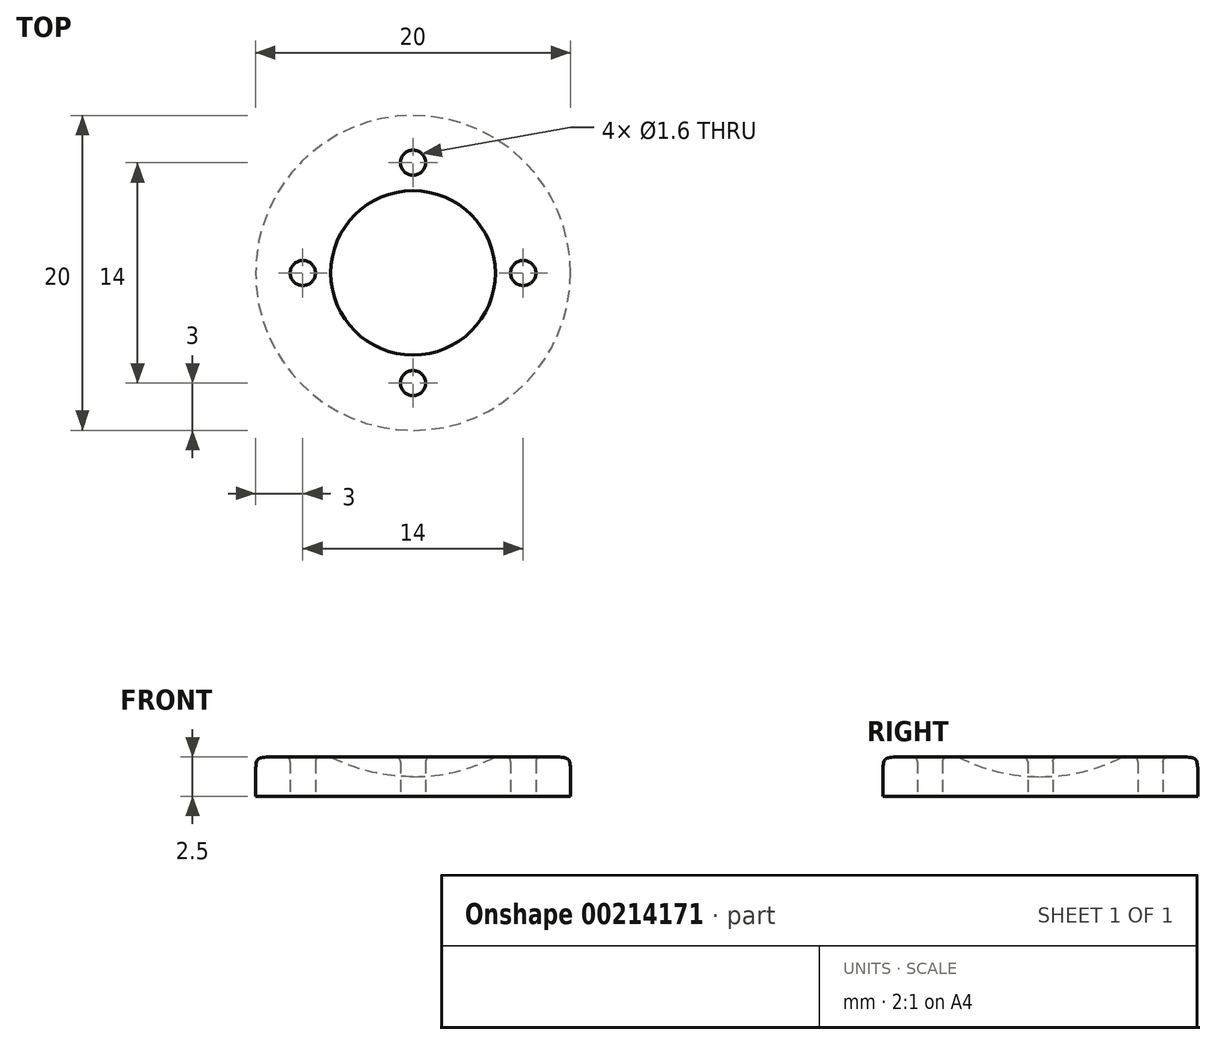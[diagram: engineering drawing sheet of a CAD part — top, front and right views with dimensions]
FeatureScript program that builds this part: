
annotation { "Feature Type Name" : "Feature", "Feature Type Description" : "" }
export const myFeature = defineFeature(function(context is Context, id is Id, definition is map)
    precondition{}
    {
        {
            var Q0;
            Q0=qCreatedBy(makeId("Top.planeOp"),FACE);
            var sketch = newSketch(context, id + "F0", { "sketchPlane" : qUnion([Q0])});
            skCircle(sketch, "E0", {"center": v(0, 0) * mm, "radius": 10 * mm});
            skCircle(sketch, "E1", {"center": v(0, 0) * mm, "radius": 7 * mm, "construction": true});
            skCircle(sketch, "E2", {"center": v(-7, 0) * mm, "radius": 0.8 * mm});
            skCircle(sketch, "E3.1.0", {"center": v(0, -7) * mm, "radius": 0.8 * mm});
            skCircle(sketch, "E3.2.0", {"center": v(7, 0) * mm, "radius": 0.8 * mm});
            skCircle(sketch, "E4.1.3.0", {"center": v(0, 7) * mm, "radius": 0.8 * mm});
            skSolve(sketch);
        }
        {
            var Q0;
            Q0=makeQuery(id+"F0.imprint","IMPRINT",FACE,{"disambiguationData":[TD([[makeQuery(id+"F0.imprint","IMPRINT",EDGE,{"derivedFrom":sQuery(id+"F0.wireOp",EDGE,"E0")}),1.0]])]});
            extrude(context, id + "F1", {"entities" : qUnion([Q0]), "depth" : 2.5 * mm});
        }
        {
            var Q0;
            Q0=qCreatedBy(makeId("Front.planeOp"),FACE);
            var sketch = newSketch(context, id + "F2", { "sketchPlane" : qUnion([Q0])});
            skLineSegment(sketch, "E5.0", {"start": v(-10, 2.5) * mm, "end": v(10, 2.5) * mm});
            skLineSegment(sketch, "E6", {"start": v(-10, 2.5) * mm, "end": v(0, 12.8) * mm, "construction": true});
            skCircle(sketch, "E7", {"center": v(0, 12.8) * mm, "radius": 11.55 * mm});
            skLineSegment(sketch, "E8", {"start": v(0, 0) * mm, "end": v(0, 2.5) * mm, "construction": true});
            skLineSegment(sketch, "E9", {"start": v(0, 1.25) * mm, "end": v(2.32, 1.25) * mm, "construction": true});
            skPoint(sketch, "E9.endSnap0", {"position": v(0, 1.25) * mm});
            skLineSegment(sketch, "E10", {"start": v(0, 1.25) * mm, "end": v(0, 24.34) * mm});
            skSolve(sketch);
        }
        {
            var Q0;
            {var subQ0=sQuery(id+"F2.wireOp",EDGE,"E7");var subQ1=sQuery(id+"F2.wireOp",EDGE,"E5.0");var subQ2=makeQuery(id+"F2.imprint","INTERSECT",VERTEX,{"disambiguationData":[OD(1.0)],"derivedFrom":[subQ1,subQ0]});Q0=makeQuery(id+"F2.imprint","IMPRINT",FACE,{"disambiguationData":[TD([[makeQuery(id+"F2.imprint","IMPRINT",EDGE,{"disambiguationData":[TD([[subQ2,1.0]])],"derivedFrom":subQ1}),-1.0]])]});}
            var Q1;
            Q1=makeQuery(id+"F1.opExtrude","CAP_EDGE",EDGE,{"disambiguationData":[OSD([sQuery(id+"F0.wireOp",EDGE,"E0")])],"isStart":false});
            revolve(context, id + "F3", {"operationType" : NewBodyOperationType.REMOVE, "entities" : qUnion([Q0]), "axis" : qUnion([Q1]), "revolveType" : RevolveType.FULL, "oppositeDirection" : true});
        }
        {
            var Q0;
            Q0=makeQuery(id+"F1.opExtrude","CAP_EDGE",EDGE,{"disambiguationData":[OSD([sQuery(id+"F0.wireOp",EDGE,"E0")])],"isStart":false});
            fillet(context, id + "F4", {"entities" : qUnion([Q0]), "radius" : 1 * mm, "tangentPropagation" : true, "rho" : 0.7, "crossSection" : FilletCrossSection.CONIC, "allowEdgeOverflow" : false});
        }
        {
            var Q0;
            Q0=makeQuery(id+"F1.opExtrude","CAP_EDGE",EDGE,{"disambiguationData":[OSD([sQuery(id+"F0.wireOp",EDGE,"E4.1.3.0")])],"isStart":false});
            var Q1;
            Q1=makeQuery(id+"F1.opExtrude","CAP_EDGE",EDGE,{"disambiguationData":[OSD([sQuery(id+"F0.wireOp",EDGE,"E3.2.0")])],"isStart":false});
            var Q2;
            Q2=makeQuery(id+"F1.opExtrude","CAP_EDGE",EDGE,{"disambiguationData":[OSD([sQuery(id+"F0.wireOp",EDGE,"E3.1.0")])],"isStart":false});
            var Q3;
            Q3=makeQuery(id+"F1.opExtrude","CAP_EDGE",EDGE,{"disambiguationData":[OSD([sQuery(id+"F0.wireOp",EDGE,"E2")])],"isStart":false});
            fillet(context, id + "F5", {"entities" : qUnion([Q0, Q1, Q2, Q3]), "radius" : 0.3 * mm, "tangentPropagation" : true, "allowEdgeOverflow" : false});
        }
    });
